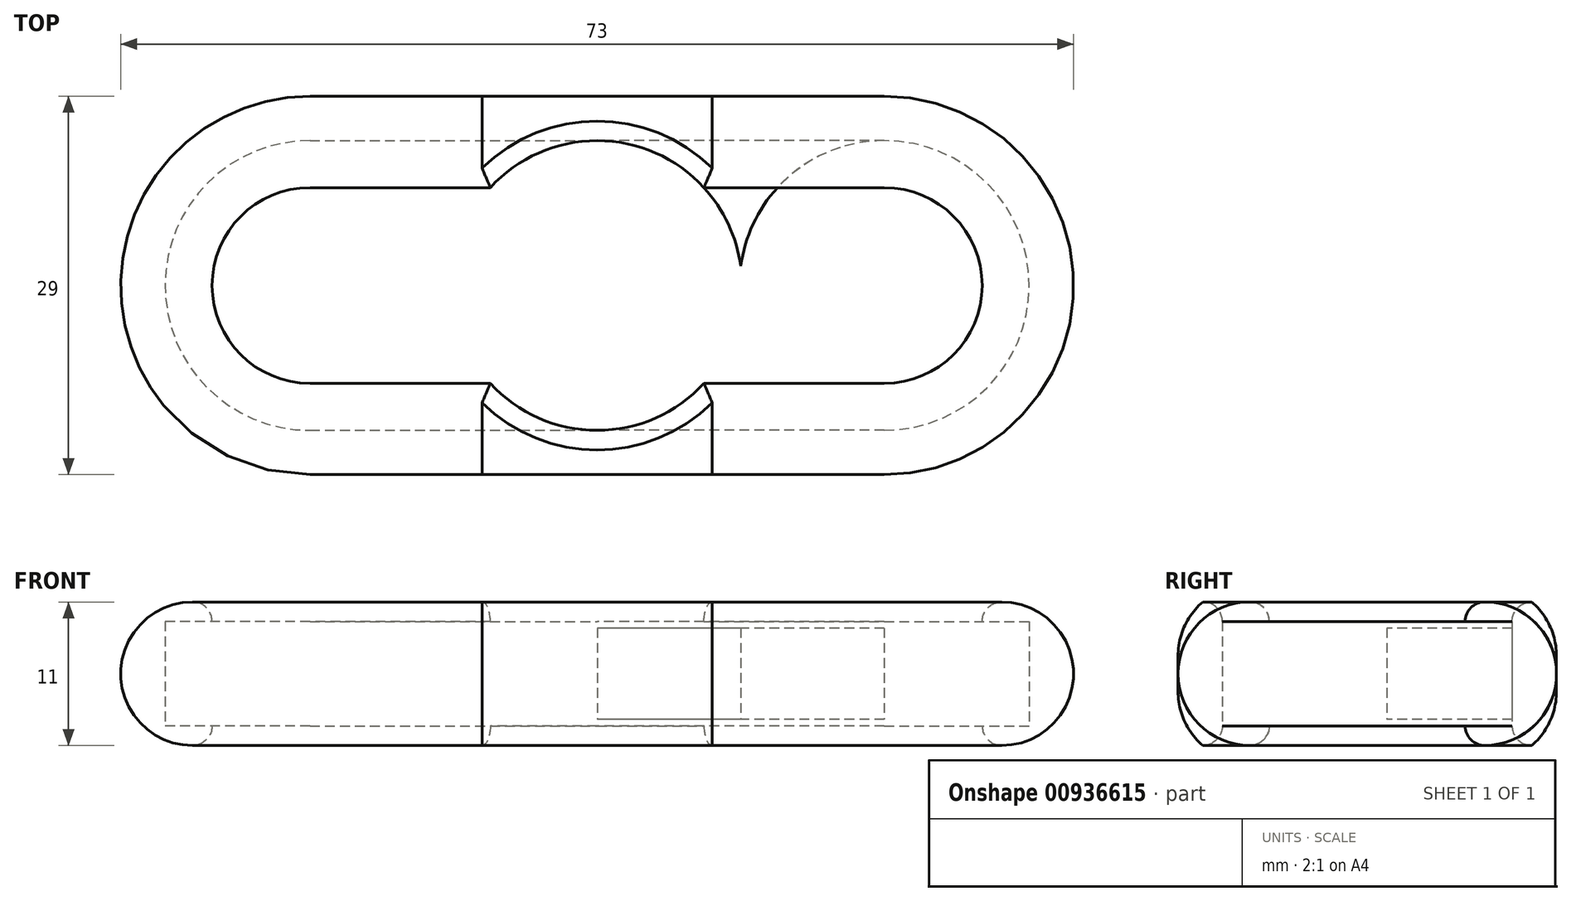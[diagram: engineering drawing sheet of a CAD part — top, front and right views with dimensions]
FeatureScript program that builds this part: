
annotation { "Feature Type Name" : "Feature", "Feature Type Description" : "" }
export const myFeature = defineFeature(function(context is Context, id is Id, definition is map)
    precondition{}
    {
        {
            var Q0;
            Q0=qCreatedBy(makeId("Top.planeOp"),FACE);
            var sketch = newSketch(context, id + "F0", { "sketchPlane" : qUnion([Q0])});
            skCircle(sketch, "E0", {"center": v(22, 0) * mm, "radius": 11.1 * mm});
            skLineSegment(sketch, "E1", {"start": v(22, 0) * mm, "end": v(22, 11.1) * mm, "construction": true});
            skLineSegment(sketch, "E2", {"start": v(22, 11.1) * mm, "end": v(0, 11.1) * mm});
            skLineSegment(sketch, "E3", {"start": v(22, 0) * mm, "end": v(22, -11.1) * mm, "construction": true});
            skLineSegment(sketch, "E4", {"start": v(22, -11.1) * mm, "end": v(0, -11.1) * mm});
            skCircle(sketch, "E5", {"center": v(22, 0) * mm, "radius": 14.5 * mm});
            skLineSegment(sketch, "E6", {"start": v(22, 0) * mm, "end": v(22, 14.5) * mm, "construction": true});
            skLineSegment(sketch, "E7", {"start": v(22, 14.5) * mm, "end": v(0, 14.5) * mm});
            skLineSegment(sketch, "E8", {"start": v(22, -11.1) * mm, "end": v(22, -14.5) * mm, "construction": true});
            skLineSegment(sketch, "E9", {"start": v(22, -14.5) * mm, "end": v(0, -14.5) * mm});
            skLineSegment(sketch, "E10", {"start": v(0, 14.5) * mm, "end": v(0, 11.1) * mm});
            skLineSegment(sketch, "E11", {"start": v(0, -11.1) * mm, "end": v(0, -14.5) * mm});
            skCircle(sketch, "E12", {"center": v(0, 0) * mm, "radius": 11.1 * mm});
            skLineSegment(sketch, "E13", {"start": v(0, 11.1) * mm, "end": v(0, -11.1) * mm});
            skCircle(sketch, "E14", {"center": v(0, 0) * mm, "radius": 7.5 * mm});
            skCircle(sketch, "E15", {"center": v(22, 0) * mm, "radius": 7.5 * mm});
            skLineSegment(sketch, "E16", {"start": v(0, -7.5) * mm, "end": v(22, -7.5) * mm});
            skLineSegment(sketch, "E17", {"start": v(22, 7.5) * mm, "end": v(0, 7.5) * mm});
            skSolve(sketch);
        }
        {
            var Q0;
            Q0=qCreatedBy(makeId("Front.planeOp"),FACE);
            var sketch = newSketch(context, id + "F1", { "sketchPlane" : qUnion([Q0])});
            skLineSegment(sketch, "E18", {"start": v(0, 0) * mm, "end": v(0, 56.46) * mm, "construction": true});
            skSolve(sketch);
        }
        {
            var Q0;
            {var subQ4=sQuery(id+"F0.wireOp",EDGE,"E7");Q0=makeQuery(id+"F0.imprint","IMPRINT",FACE,{"disambiguationData":[TD([[makeQuery(id+"F0.imprint","IMPRINT",EDGE,{"derivedFrom":subQ4}),1.0]])]});}
            var Q1;
            {var subQ1=sQuery(id+"F0.wireOp",EDGE,"E2");var subQ3=sQuery(id+"F0.wireOp",EDGE,"E5");var subQ4=makeQuery(id+"F0.imprint","INTERSECT",VERTEX,{"derivedFrom":[subQ1,subQ3]});Q1=makeQuery(id+"F0.imprint","IMPRINT",FACE,{"disambiguationData":[TD([[makeQuery(id+"F0.imprint","IMPRINT",EDGE,{"disambiguationData":[TD([[subQ4,-1.0]])],"derivedFrom":subQ3}),-1.0]])]});}
            var Q2;
            {var subQ0=sQuery(id+"F0.wireOp",EDGE,"E2");var subQ1=sQuery(id+"F0.wireOp",EDGE,"E0");var subQ2=makeQuery(id+"F0.imprint","INTERSECT",VERTEX,{"derivedFrom":[subQ1,subQ0]});Q2=makeQuery(id+"F0.imprint","IMPRINT",FACE,{"disambiguationData":[TD([[makeQuery(id+"F0.imprint","IMPRINT",EDGE,{"disambiguationData":[TD([[subQ2,-1.0]])],"derivedFrom":subQ1}),-1.0]])]});}
            var Q3;
            {var subQ0=sQuery(id+"F0.wireOp",EDGE,"E4");var subQ1=sQuery(id+"F0.wireOp",EDGE,"E0");var subQ2=makeQuery(id+"F0.imprint","INTERSECT",VERTEX,{"derivedFrom":[subQ1,subQ0]});Q3=makeQuery(id+"F0.imprint","IMPRINT",FACE,{"disambiguationData":[TD([[makeQuery(id+"F0.imprint","IMPRINT",EDGE,{"disambiguationData":[TD([[subQ2,1.0]])],"derivedFrom":subQ1}),-1.0]])]});}
            var Q4;
            {var subQ1=sQuery(id+"F0.wireOp",EDGE,"E4");var subQ3=sQuery(id+"F0.wireOp",EDGE,"E5");var subQ4=makeQuery(id+"F0.imprint","INTERSECT",VERTEX,{"derivedFrom":[subQ1,subQ3]});Q4=makeQuery(id+"F0.imprint","IMPRINT",FACE,{"disambiguationData":[TD([[makeQuery(id+"F0.imprint","IMPRINT",EDGE,{"disambiguationData":[TD([[subQ4,1.0]])],"derivedFrom":subQ3}),-1.0]])]});}
            var Q5;
            {var subQ4=sQuery(id+"F0.wireOp",EDGE,"E9");Q5=makeQuery(id+"F0.imprint","IMPRINT",FACE,{"disambiguationData":[TD([[makeQuery(id+"F0.imprint","IMPRINT",EDGE,{"derivedFrom":subQ4}),-1.0]])]});}
            var Q6;
            {var subQ1=sQuery(id+"F0.wireOp",EDGE,"E0");var subQ5=sQuery(id+"F0.wireOp",EDGE,"E2");var subQ6=makeQuery(id+"F0.imprint","INTERSECT",VERTEX,{"derivedFrom":[subQ1,subQ5]});Q6=makeQuery(id+"F0.imprint","IMPRINT",FACE,{"disambiguationData":[TD([[makeQuery(id+"F0.imprint","IMPRINT",EDGE,{"disambiguationData":[TD([[subQ6,1.0]])],"derivedFrom":subQ1}),-1.0]])]});}
            var Q7;
            {var subQ0=sQuery(id+"F0.wireOp",EDGE,"E0");var subQ1=makeQuery(id+"F0.imprint","INTERSECT",VERTEX,{"derivedFrom":[subQ0,sQuery(id+"F0.wireOp",EDGE,"E2")]});Q7=makeQuery(id+"F0.imprint","IMPRINT",FACE,{"disambiguationData":[TD([[makeQuery(id+"F0.imprint","IMPRINT",EDGE,{"disambiguationData":[TD([[subQ1,-1.0]])],"derivedFrom":subQ0}),1.0]])]});}
            extrude(context, id + "F2", {"entities" : qUnion([Q0, Q1, Q2, Q3, Q4, Q5, Q6, Q7]), "endBound" : BoundingType.SYMMETRIC, "depth" : 11 * mm, "offsetDistance" : 25 * mm});
        }
        {
            var Q0;
            {var subQ1=sQuery(id+"F0.wireOp",EDGE,"E2");var subQ3=sQuery(id+"F0.wireOp",EDGE,"E5");var subQ4=makeQuery(id+"F0.imprint","INTERSECT",VERTEX,{"derivedFrom":[subQ1,subQ3]});Q0=makeQuery(id+"F0.imprint","IMPRINT",FACE,{"disambiguationData":[TD([[makeQuery(id+"F0.imprint","IMPRINT",EDGE,{"disambiguationData":[TD([[subQ4,-1.0]])],"derivedFrom":subQ3}),-1.0]])]});}
            var Q1;
            {var subQ0=sQuery(id+"F0.wireOp",EDGE,"E2");var subQ1=sQuery(id+"F0.wireOp",EDGE,"E0");var subQ2=makeQuery(id+"F0.imprint","INTERSECT",VERTEX,{"derivedFrom":[subQ1,subQ0]});Q1=makeQuery(id+"F0.imprint","IMPRINT",FACE,{"disambiguationData":[TD([[makeQuery(id+"F0.imprint","IMPRINT",EDGE,{"disambiguationData":[TD([[subQ2,-1.0]])],"derivedFrom":subQ1}),-1.0]])]});}
            var Q2;
            {var subQ0=sQuery(id+"F0.wireOp",EDGE,"E0");var subQ1=makeQuery(id+"F0.imprint","INTERSECT",VERTEX,{"derivedFrom":[subQ0,sQuery(id+"F0.wireOp",EDGE,"E2")]});Q2=makeQuery(id+"F0.imprint","IMPRINT",FACE,{"disambiguationData":[TD([[makeQuery(id+"F0.imprint","IMPRINT",EDGE,{"disambiguationData":[TD([[subQ1,-1.0]])],"derivedFrom":subQ0}),1.0]])]});}
            var Q3;
            {var subQ0=sQuery(id+"F0.wireOp",EDGE,"E4");var subQ1=sQuery(id+"F0.wireOp",EDGE,"E0");var subQ2=makeQuery(id+"F0.imprint","INTERSECT",VERTEX,{"derivedFrom":[subQ1,subQ0]});Q3=makeQuery(id+"F0.imprint","IMPRINT",FACE,{"disambiguationData":[TD([[makeQuery(id+"F0.imprint","IMPRINT",EDGE,{"disambiguationData":[TD([[subQ2,1.0]])],"derivedFrom":subQ1}),-1.0]])]});}
            var Q4;
            {var subQ1=sQuery(id+"F0.wireOp",EDGE,"E4");var subQ3=sQuery(id+"F0.wireOp",EDGE,"E5");var subQ4=makeQuery(id+"F0.imprint","INTERSECT",VERTEX,{"derivedFrom":[subQ1,subQ3]});Q4=makeQuery(id+"F0.imprint","IMPRINT",FACE,{"disambiguationData":[TD([[makeQuery(id+"F0.imprint","IMPRINT",EDGE,{"disambiguationData":[TD([[subQ4,1.0]])],"derivedFrom":subQ3}),-1.0]])]});}
            var Q5;
            {var subQ0=sQuery(id+"F0.wireOp",EDGE,"E12");var subQ1=sQuery(id+"F0.wireOp",EDGE,"E0");var subQ2=makeQuery(id+"F0.imprint","INTERSECT",VERTEX,{"disambiguationData":[OD(0.0)],"derivedFrom":[subQ1,subQ0]});Q5=makeQuery(id+"F0.imprint","IMPRINT",FACE,{"disambiguationData":[TD([[makeQuery(id+"F0.imprint","IMPRINT",EDGE,{"disambiguationData":[TD([[subQ2,-1.0]])],"derivedFrom":subQ1}),-1.0]])]});}
            var Q6;
            {var subQ4=sQuery(id+"F0.wireOp",EDGE,"E13");Q6=makeQuery(id+"F0.imprint","IMPRINT",FACE,{"disambiguationData":[TD([[makeQuery(id+"F0.imprint","IMPRINT",EDGE,{"derivedFrom":subQ4}),1.0]])]});}
            extrude(context, id + "F3", {"entities" : qUnion([Q0, Q1, Q2, Q3, Q4, Q5, Q6]), "operationType" : NewBodyOperationType.REMOVE, "endBound" : BoundingType.SYMMETRIC, "depth" : 8 * mm, "offsetDistance" : 25 * mm});
        }
        {
            var Q0;
            Q0=makeQuery(id+"F2.opExtrude","SWEPT_BODY",BODY,{"disambiguationData":[OSD([sQuery(id+"F0.wireOp",EDGE,"E5"),sQuery(id+"F0.wireOp",EDGE,"E7"),sQuery(id+"F0.wireOp",EDGE,"E9"),sQuery(id+"F0.wireOp",EDGE,"E10"),sQuery(id+"F0.wireOp",EDGE,"E11"),sQuery(id+"F0.wireOp",EDGE,"E12")])]});
            var Q1;
            Q1=sQuery(id+"F1.wireOp",EDGE,"E18");
            circularPattern(context, id + "F4", {"operationType" : NewBodyOperationType.ADD, "entities" : qUnion([Q0]), "axis" : qUnion([Q1]), "angle" : 360 * degree, "instanceCount" : 2, "equalSpace" : true});
        }
        {
            var Q0;
            {var subQ0=makeQuery(id+"F2.opExtrude","CAP_EDGE",EDGE,{"disambiguationData":[OSD([sQuery(id+"F0.wireOp",EDGE,"E12")])],"isStart":false});Q0=makeQuery(id+"F4.boolean.opBoolean","MERGE",EDGE,{"derivedFrom":[subQ0,makeQuery(id+"F4.opPattern","COPY",EDGE,{"derivedFrom":subQ0,"instanceName":"1"})]});}
            var Q1;
            {var subQ0=makeQuery(id+"F2.opExtrude","CAP_EDGE",EDGE,{"disambiguationData":[OSD([sQuery(id+"F0.wireOp",EDGE,"E12")])],"isStart":true});Q1=makeQuery(id+"F4.boolean.opBoolean","MERGE",EDGE,{"derivedFrom":[subQ0,makeQuery(id+"F4.opPattern","COPY",EDGE,{"derivedFrom":subQ0,"instanceName":"1"})]});}
            var Q2;
            Q2=makeQuery(id+"F4.opPattern","COPY",EDGE,{"derivedFrom":makeQuery(id+"F2.opExtrude","CAP_EDGE",EDGE,{"disambiguationData":[OSD([sQuery(id+"F0.wireOp",EDGE,"E16")])],"isStart":false}),"instanceName":"1"});
            var Q3;
            Q3=makeQuery(id+"F2.opExtrude","CAP_EDGE",EDGE,{"disambiguationData":[OSD([sQuery(id+"F0.wireOp",EDGE,"E17")])],"isStart":false});
            var Q4;
            Q4=makeQuery(id+"F2.opExtrude","CAP_EDGE",EDGE,{"disambiguationData":[OSD([sQuery(id+"F0.wireOp",EDGE,"E17")])],"isStart":true});
            var Q5;
            Q5=makeQuery(id+"F4.opPattern","COPY",EDGE,{"derivedFrom":makeQuery(id+"F2.opExtrude","CAP_EDGE",EDGE,{"disambiguationData":[OSD([sQuery(id+"F0.wireOp",EDGE,"E16")])],"isStart":true}),"instanceName":"1"});
            fillet(context, id + "F5", {"entities" : qUnion([Q0, Q1, Q2, Q3, Q4, Q5]), "radius" : 1.5 * mm, "tangentPropagation" : true, "allowEdgeOverflow" : false});
        }
        {
            var Q0;
            Q0=makeQuery(id+"F2.opExtrude","CAP_EDGE",EDGE,{"disambiguationData":[OSD([sQuery(id+"F0.wireOp",EDGE,"E5")])],"isStart":false});
            var Q1;
            Q1=makeQuery(id+"F2.opExtrude","CAP_EDGE",EDGE,{"disambiguationData":[OSD([sQuery(id+"F0.wireOp",EDGE,"E5")])],"isStart":true});
            fillet(context, id + "F6", {"entities" : qUnion([Q0, Q1]), "radius" : 5.5 * mm, "tangentPropagation" : true, "allowEdgeOverflow" : false});
        }
        {
            var Q0;
            {var subQ1=sQuery(id+"F0.wireOp",EDGE,"E2");var subQ3=sQuery(id+"F0.wireOp",EDGE,"E5");var subQ4=makeQuery(id+"F0.imprint","INTERSECT",VERTEX,{"derivedFrom":[subQ1,subQ3]});Q0=makeQuery(id+"F0.imprint","IMPRINT",FACE,{"disambiguationData":[TD([[makeQuery(id+"F0.imprint","IMPRINT",EDGE,{"disambiguationData":[TD([[subQ4,-1.0]])],"derivedFrom":subQ3}),-1.0]])]});}
            var Q1;
            {var subQ0=sQuery(id+"F0.wireOp",EDGE,"E17");var subQ1=sQuery(id+"F0.wireOp",EDGE,"E5");var subQ2=makeQuery(id+"F0.imprint","INTERSECT",VERTEX,{"derivedFrom":[subQ1,subQ0]});Q1=makeQuery(id+"F0.imprint","IMPRINT",FACE,{"disambiguationData":[TD([[makeQuery(id+"F0.imprint","IMPRINT",EDGE,{"disambiguationData":[TD([[subQ2,-1.0]])],"derivedFrom":subQ1}),-1.0]])]});}
            var Q2;
            {var subQ0=sQuery(id+"F0.wireOp",EDGE,"E2");var subQ1=sQuery(id+"F0.wireOp",EDGE,"E0");var subQ2=makeQuery(id+"F0.imprint","INTERSECT",VERTEX,{"derivedFrom":[subQ1,subQ0]});Q2=makeQuery(id+"F0.imprint","IMPRINT",FACE,{"disambiguationData":[TD([[makeQuery(id+"F0.imprint","IMPRINT",EDGE,{"disambiguationData":[TD([[subQ2,-1.0]])],"derivedFrom":subQ1}),-1.0]])]});}
            var Q3;
            {var subQ0=sQuery(id+"F0.wireOp",EDGE,"E17");var subQ1=sQuery(id+"F0.wireOp",EDGE,"E0");var subQ2=makeQuery(id+"F0.imprint","INTERSECT",VERTEX,{"derivedFrom":[subQ1,subQ0]});Q3=makeQuery(id+"F0.imprint","IMPRINT",FACE,{"disambiguationData":[TD([[makeQuery(id+"F0.imprint","IMPRINT",EDGE,{"disambiguationData":[TD([[subQ2,-1.0]])],"derivedFrom":subQ1}),-1.0]])]});}
            extrude(context, id + "F7", {"entities" : qUnion([Q0, Q1, Q2, Q3]), "endBound" : BoundingType.SYMMETRIC, "depth" : 7 * mm, "offsetDistance" : 25 * mm});
        }
    });
